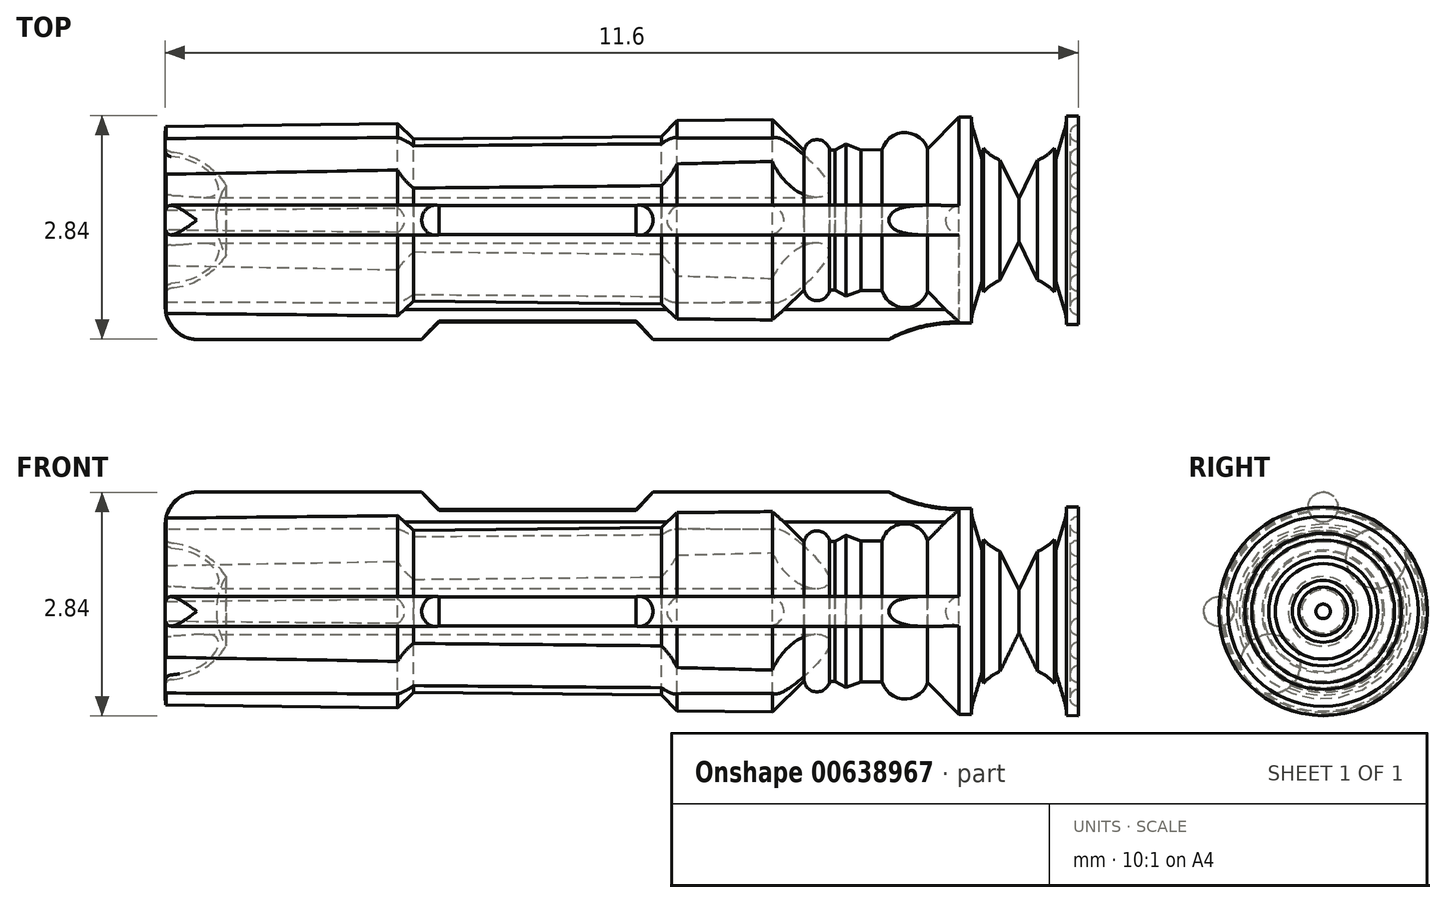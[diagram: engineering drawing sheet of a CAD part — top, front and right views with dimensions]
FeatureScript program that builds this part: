
annotation { "Feature Type Name" : "Feature", "Feature Type Description" : "" }
export const myFeature = defineFeature(function(context is Context, id is Id, definition is map)
    precondition{}
    {
        {
            var Q0;
            Q0=qCreatedBy(makeId("Top.planeOp"),FACE);
            var sketch = newSketch(context, id + "F0", { "sketchPlane" : qUnion([Q0])});
            skLineSegment(sketch, "E0", {"start": v(0, 6) * mm, "end": v(0, -4.69) * mm});
            skLineSegment(sketch, "E1", {"start": v(0, 6) * mm, "end": v(1.33, 6) * mm});
            skLineSegment(sketch, "E2", {"start": v(1.33, 6) * mm, "end": v(1.3, 4.48) * mm});
            skLineSegment(sketch, "E3", {"start": v(1.2, -5.6) * mm, "end": v(0.95, -5.6) * mm});
            skArc(sketch, "E4", {"start": v(0.87, -5.52) * mm, "mid": v(0.74, -5.12) * mm, "end": v(0.44, -4.83) * mm});
            skLineSegment(sketch, "E5", {"start": v(0.87, -5.6) * mm, "end": v(0, -5.6) * mm, "construction": true});
            skLineSegment(sketch, "E6", {"start": v(0, -4.69) * mm, "end": v(0, -4.95) * mm});
            skPoint(sketch, "E7.visualSharp", {"position": v(0.87, -5.6) * mm});
            skArc(sketch, "E7.filletArc", {"start": v(0.87, -5.52) * mm, "mid": v(0.9, -5.58) * mm, "end": v(0.95, -5.6) * mm});
            skLineSegment(sketch, "E8", {"start": v(0, 0) * mm, "end": v(1.26, 0) * mm, "construction": true});
            skArc(sketch, "E9", {"start": v(0, -4.95) * mm, "mid": v(0.23, -4.92) * mm, "end": v(0.44, -4.83) * mm});
            skLineSegment(sketch, "E10", {"start": v(0, -4.95) * mm, "end": v(0, -5.6) * mm, "construction": true});
            skArc(sketch, "E11", {"start": v(0.44, -4.83) * mm, "mid": v(0.23, -4.73) * mm, "end": v(0, -4.69) * mm, "construction": true});
            skArc(sketch, "E12", {"start": v(0.44, -4.83) * mm, "mid": v(0.52, -4.77) * mm, "end": v(0.59, -4.72) * mm, "construction": true});
            skArc(sketch, "E13", {"start": v(0.1, 6) * mm, "mid": v(0.2, 5.9) * mm, "end": v(0.3, 6) * mm});
            skArc(sketch, "E14.1.0.0", {"start": v(0.4, 6) * mm, "mid": v(0.5, 5.9) * mm, "end": v(0.6, 6) * mm});
            skArc(sketch, "E14.2.0.0", {"start": v(0.7, 6) * mm, "mid": v(0.8, 5.9) * mm, "end": v(0.9, 6) * mm});
            skArc(sketch, "E14.3.0.0", {"start": v(1, 6) * mm, "mid": v(1.1, 5.9) * mm, "end": v(1.2, 6) * mm});
            skLineSegment(sketch, "E14.direction1", {"start": v(0.1, 6) * mm, "end": v(0.4, 6) * mm, "construction": true});
            skArc(sketch, "E15.0", {"start": v(1, -5.2) * mm, "mid": v(0.77, -4.84) * mm, "end": v(0.43, -4.6) * mm, "construction": true});
            skLineSegment(sketch, "E15.1", {"start": v(1.12, 5.8) * mm, "end": v(1.1, 4.28) * mm, "construction": true});
            skArc(sketch, "E15.2", {"start": v(0.2, -4.72) * mm, "mid": v(0.32, -4.67) * mm, "end": v(0.43, -4.6) * mm, "construction": true});
            skLineSegment(sketch, "E16.0", {"start": v(0.92, 5.8) * mm, "end": v(0.9, 4.09) * mm, "construction": true});
            skLineSegment(sketch, "E17", {"start": v(1.23, -2.65) * mm, "end": v(1.03, -2.45) * mm});
            skLineSegment(sketch, "E18", {"start": v(1.06, 0.7) * mm, "end": v(1.27, 0.9) * mm});
            skLineSegment(sketch, "E19", {"start": v(1.03, -2.45) * mm, "end": v(1, -5.2) * mm, "construction": true});
            skLineSegment(sketch, "E20", {"start": v(1.06, 0.7) * mm, "end": v(1.03, -2.45) * mm});
            skLineSegment(sketch, "E21", {"start": v(1.23, -2.65) * mm, "end": v(1.2, -5.6) * mm});
            skLineSegment(sketch, "E22", {"start": v(1.27, 0.9) * mm, "end": v(1.23, -2.65) * mm, "construction": true});
            skLineSegment(sketch, "E23", {"start": v(1.28, 2.11) * mm, "end": v(1.08, 2.32) * mm});
            skLineSegment(sketch, "E24", {"start": v(1.3, 4.48) * mm, "end": v(1.1, 4.28) * mm});
            skLineSegment(sketch, "E25", {"start": v(0.88, 2.52) * mm, "end": v(0.8, -5.13) * mm, "construction": true});
            skLineSegment(sketch, "E26", {"start": v(0.9, 4.09) * mm, "end": v(0.9, 3.24) * mm});
            skLineSegment(sketch, "E27", {"start": v(1.08, 2.32) * mm, "end": v(0.88, 2.52) * mm});
            skLineSegment(sketch, "E28", {"start": v(1.1, 4.28) * mm, "end": v(0.9, 4.09) * mm});
            skLineSegment(sketch, "E29", {"start": v(1.08, 2.32) * mm, "end": v(1.06, 0.7) * mm, "construction": true});
            skLineSegment(sketch, "E30", {"start": v(1.1, 4.28) * mm, "end": v(1.08, 2.32) * mm, "construction": true});
            skLineSegment(sketch, "E31", {"start": v(1.28, 2.11) * mm, "end": v(1.27, 0.9) * mm});
            skLineSegment(sketch, "E32", {"start": v(1.3, 4.48) * mm, "end": v(1.28, 2.11) * mm, "construction": true});
            skArc(sketch, "E33", {"start": v(0.88, 2.52) * mm, "mid": v(1.02, 2.68) * mm, "end": v(0.89, 2.84) * mm});
            skArc(sketch, "E34", {"start": v(0.9, 3.5) * mm, "mid": v(1.11, 3.8) * mm, "end": v(0.9, 4.09) * mm});
            skLineSegment(sketch, "E35", {"start": v(0.89, 2.91) * mm, "end": v(0.89, 2.84) * mm});
            skLineSegment(sketch, "E36", {"start": v(0.97, 3.05) * mm, "end": v(0.89, 2.91) * mm});
            skLineSegment(sketch, "E37", {"start": v(0.9, 3.24) * mm, "end": v(0.97, 3.05) * mm});
            skLineSegment(sketch, "E38", {"start": v(0.89, 2.84) * mm, "end": v(0.88, 2.52) * mm});
            skSolve(sketch);
        }
        {
            var Q0;
            {var subQ5=sQuery(id+"F0.wireOp",EDGE,"E0");Q0=makeQuery(id+"F0.imprint","IMPRINT",FACE,{"disambiguationData":[TD([[makeQuery(id+"F0.imprint","IMPRINT",EDGE,{"derivedFrom":subQ5}),1.0]])]});}
            var Q1;
            Q1=makeQuery(id+"F0.imprint","IMPRINT",FACE,{"disambiguationData":[TD([[makeQuery(id+"F0.imprint","IMPRINT",EDGE,{"derivedFrom":sQuery(id+"F0.wireOp",EDGE,"E33")}),1.0]])]});
            var Q2;
            {var subQ0=sQuery(id+"F0.wireOp",EDGE,"E34");Q2=makeQuery(id+"F0.imprint","IMPRINT",FACE,{"disambiguationData":[TD([[makeQuery(id+"F0.imprint","IMPRINT",EDGE,{"derivedFrom":subQ0}),1.0]])]});}
            var Q3;
            Q3=sQuery(id+"F0.wireOp",EDGE,"E0");
            revolve(context, id + "F1", {"entities" : qUnion([Q0, Q1, Q2]), "axis" : qUnion([Q3]), "revolveType" : RevolveType.FULL});
        }
        {
            var Q0;
            Q0=qCreatedBy(makeId("Front.planeOp"),FACE);
            var sketch = newSketch(context, id + "F2", { "sketchPlane" : qUnion([Q0])});
            skLineSegment(sketch, "E39", {"start": v(0, 0) * mm, "end": v(0, 0.95) * mm, "construction": true});
            skLineSegment(sketch, "E40", {"start": v(0, 0) * mm, "end": v(-1.33, 0) * mm, "construction": true});
            skArc(sketch, "E41", {"start": v(-0.95, 0) * mm, "mid": v(-0.87, 0.36) * mm, "end": v(-0.67, 0.67) * mm, "construction": true});
            skArc(sketch, "E42", {"start": v(0, 0.95) * mm, "mid": v(0.67, -0.67) * mm, "end": v(-0.95, 0) * mm, "construction": true});
            skArc(sketch, "E43", {"start": v(0, 1.33) * mm, "mid": v(0.94, -0.94) * mm, "end": v(-1.33, 0) * mm, "construction": true});
            skArc(sketch, "E44", {"start": v(-1.33, 0) * mm, "mid": v(-1.22, 0.5) * mm, "end": v(-0.94, 0.94) * mm, "construction": true});
            skLineSegment(sketch, "E45", {"start": v(0, 0) * mm, "end": v(-0.94, 0.94) * mm, "construction": true});
            skArc(sketch, "E46", {"start": v(-0.94, 0.94) * mm, "mid": v(-0.5, 1.22) * mm, "end": v(0, 1.33) * mm, "construction": true});
            skArc(sketch, "E47", {"start": v(-0.67, 0.67) * mm, "mid": v(-0.36, 0.87) * mm, "end": v(0, 0.95) * mm, "construction": true});
            skCircle(sketch, "E48", {"center": v(-0.67, 0.67) * mm, "radius": 0.38 * mm});
            skCircle(sketch, "E49.MirrorC", {"center": v(0.67, 0.67) * mm, "radius": 0.38 * mm});
            skCircle(sketch, "E50.MirrorC", {"center": v(-0.67, -0.67) * mm, "radius": 0.38 * mm});
            skCircle(sketch, "E51.MirrorC", {"center": v(0.67, -0.67) * mm, "radius": 0.38 * mm});
            skCircle(sketch, "E52", {"center": v(0, 1.33) * mm, "radius": 0.19 * mm});
            skLineSegment(sketch, "E53", {"start": v(0, 0.95) * mm, "end": v(0, 1.33) * mm, "construction": true});
            skPoint(sketch, "E54", {"position": v(0, 1.14) * mm});
            skCircle(sketch, "E55.MirrorC", {"center": v(0, -1.33) * mm, "radius": 0.19 * mm});
            skCircle(sketch, "E56.MirrorC", {"center": v(-1.33, 0) * mm, "radius": 0.19 * mm});
            skCircle(sketch, "E57.MirrorC", {"center": v(1.33, 0) * mm, "radius": 0.19 * mm});
            skSolve(sketch);
        }
        {
            var Q0;
            Q0=makeQuery(id+"F2.imprint","IMPRINT",FACE,{"disambiguationData":[TD([[makeQuery(id+"F2.imprint","IMPRINT",EDGE,{"derivedFrom":sQuery(id+"F2.wireOp",EDGE,"E48")}),1.0]])]});
            var Q1;
            Q1=makeQuery(id+"F2.imprint","IMPRINT",FACE,{"disambiguationData":[TD([[makeQuery(id+"F2.imprint","IMPRINT",EDGE,{"derivedFrom":sQuery(id+"F2.wireOp",EDGE,"E49.MirrorC")}),-1.0]])]});
            var Q2;
            Q2=makeQuery(id+"F2.imprint","IMPRINT",FACE,{"disambiguationData":[TD([[makeQuery(id+"F2.imprint","IMPRINT",EDGE,{"derivedFrom":sQuery(id+"F2.wireOp",EDGE,"E51.MirrorC")}),1.0]])]});
            var Q3;
            Q3=makeQuery(id+"F2.imprint","IMPRINT",FACE,{"disambiguationData":[TD([[makeQuery(id+"F2.imprint","IMPRINT",EDGE,{"derivedFrom":sQuery(id+"F2.wireOp",EDGE,"E50.MirrorC")}),-1.0]])]});
            var Q4;
            Q4=makeQuery(id+"F1.opRevolve","SWEPT_FACE",FACE,{"disambiguationData":[OSD([sQuery(id+"F0.wireOp",EDGE,"E3")])]});
            var Q5;
            Q5=makeQuery(id+"F1.opRevolve","SWEPT_FACE",FACE,{"disambiguationData":[OSD([sQuery(id+"F0.wireOp",EDGE,"E23"),sQuery(id+"F0.wireOp",EDGE,"E27")])]});
            extrude(context, id + "F3", {"entities" : qUnion([Q0, Q1, Q2, Q3]), "operationType" : NewBodyOperationType.REMOVE, "endBound" : BoundingType.UP_TO_SURFACE, "endBoundEntityFace" : qUnion([Q4]), "depth" : 5.84 * mm, "hasSecondDirection" : true, "secondDirectionBound" : SecondDirectionBoundingType.UP_TO_SURFACE, "secondDirectionOppositeDirection" : true, "secondDirectionBoundEntityFace" : qUnion([Q5]), "secondDirectionDepth" : 2.4 * mm});
        }
        {
            var Q0;
            Q0=makeQuery(id+"F2.imprint","IMPRINT",FACE,{"disambiguationData":[TD([[makeQuery(id+"F2.imprint","IMPRINT",EDGE,{"derivedFrom":sQuery(id+"F2.wireOp",EDGE,"E56.MirrorC")}),-1.0]])]});
            var Q1;
            Q1=makeQuery(id+"F2.imprint","IMPRINT",FACE,{"disambiguationData":[TD([[makeQuery(id+"F2.imprint","IMPRINT",EDGE,{"derivedFrom":sQuery(id+"F2.wireOp",EDGE,"E55.MirrorC")}),-1.0]])]});
            var Q2;
            Q2=makeQuery(id+"F2.imprint","IMPRINT",FACE,{"disambiguationData":[TD([[makeQuery(id+"F2.imprint","IMPRINT",EDGE,{"derivedFrom":sQuery(id+"F2.wireOp",EDGE,"E57.MirrorC")}),1.0]])]});
            var Q3;
            Q3=makeQuery(id+"F2.imprint","IMPRINT",FACE,{"disambiguationData":[TD([[makeQuery(id+"F2.imprint","IMPRINT",EDGE,{"derivedFrom":sQuery(id+"F2.wireOp",EDGE,"E52")}),1.0]])]});
            var Q4;
            Q4=makeQuery(id+"F3.boolean.opBoolean","SPLIT",FACE,{"disambiguationData":[TD([makeQuery(id+"F1.opRevolve","SWEPT_FACE",FACE,{"disambiguationData":[OSD([sQuery(id+"F0.wireOp",EDGE,"E7.filletArc")])]}),makeQuery(id+"F1.opRevolve","SWEPT_FACE",FACE,{"disambiguationData":[OSD([sQuery(id+"F0.wireOp",EDGE,"E21")])]}),makeQuery(id+"F3.opExtrude","SWEPT_FACE",FACE,{"disambiguationData":[OSD([sQuery(id+"F2.wireOp",EDGE,"E48")])]}),makeQuery(id+"F3.opExtrude","SWEPT_FACE",FACE,{"disambiguationData":[OSD([sQuery(id+"F2.wireOp",EDGE,"E49.MirrorC")])]})])],"derivedFrom":makeQuery(id+"F1.opRevolve","SWEPT_FACE",FACE,{"disambiguationData":[OSD([sQuery(id+"F0.wireOp",EDGE,"E3")])]})});
            var Q5;
            Q5=makeQuery(id+"F1.opRevolve","SWEPT_FACE",FACE,{"disambiguationData":[OSD([sQuery(id+"F0.wireOp",EDGE,"E24"),sQuery(id+"F0.wireOp",EDGE,"E28")])]});
            extrude(context, id + "F4", {"entities" : qUnion([Q0, Q1, Q2, Q3]), "operationType" : NewBodyOperationType.ADD, "endBound" : BoundingType.UP_TO_SURFACE, "endBoundEntityFace" : qUnion([Q4]), "depth" : 25 * mm, "hasSecondDirection" : true, "secondDirectionBound" : SecondDirectionBoundingType.UP_TO_SURFACE, "secondDirectionOppositeDirection" : true, "secondDirectionBoundEntityFace" : qUnion([Q5]), "secondDirectionDepth" : 25 * mm});
        }
        {
            var Q0;
            Q0=qCreatedBy(makeId("Top.planeOp"),FACE);
            var sketch = newSketch(context, id + "F5", { "sketchPlane" : qUnion([Q0])});
            skLineSegment(sketch, "E58.0", {"start": v(-1.33, 6) * mm, "end": v(1.33, 6) * mm});
            skLineSegment(sketch, "E59", {"start": v(1.33, 6) * mm, "end": v(1.32, 5.85) * mm});
            skLineSegment(sketch, "E60", {"start": v(1.51, 4.68) * mm, "end": v(1.51, 3.6) * mm, "construction": true});
            skLineSegment(sketch, "E61", {"start": v(0, 0) * mm, "end": v(0, 6) * mm});
            skLineSegment(sketch, "E62", {"start": v(0, 0) * mm, "end": v(0, -5.6) * mm});
            skLineSegment(sketch, "E63.0", {"start": v(0, -5.6) * mm, "end": v(1.11, -5.6) * mm});
            skPoint(sketch, "E64.orphan", {"position": v(0.13, -5.6) * mm});
            skPoint(sketch, "E65.orphan", {"position": v(0.58, -5.6) * mm});
            skPoint(sketch, "E66.visualSharp", {"position": v(1.51, -5.6) * mm});
            skArc(sketch, "E66.filletArc", {"start": v(1.11, -5.6) * mm, "mid": v(1.4, -5.48) * mm, "end": v(1.51, -5.2) * mm});
            skLineSegment(sketch, "E67", {"start": v(1.51, -2.34) * mm, "end": v(1.51, -5.2) * mm});
            skLineSegment(sketch, "E68", {"start": v(1.51, 0.6) * mm, "end": v(1.51, -2.34) * mm, "construction": true});
            skLineSegment(sketch, "E69", {"start": v(1.51, -2.34) * mm, "end": v(1.3, -2.12) * mm});
            skLineSegment(sketch, "E70", {"start": v(1.3, -2.12) * mm, "end": v(1.3, 0.38) * mm});
            skLineSegment(sketch, "E71", {"start": v(1.3, 0.38) * mm, "end": v(1.51, 0.6) * mm});
            skArc(sketch, "E72", {"start": v(1.3, 4.49) * mm, "mid": v(1.36, 4.03) * mm, "end": v(1.51, 3.6) * mm});
            skLineSegment(sketch, "E73", {"start": v(1.51, 3.6) * mm, "end": v(1.51, 0.6) * mm});
            skArc(sketch, "E74", {"start": v(1.32, 5.85) * mm, "mid": v(0.71, 5.25) * mm, "end": v(1.3, 4.64) * mm});
            skLineSegment(sketch, "E75", {"start": v(1.3, 4.64) * mm, "end": v(1.3, 4.49) * mm});
            skLineSegment(sketch, "E76", {"start": v(1.32, 5.85) * mm, "end": v(1.3, 4.64) * mm, "construction": true});
            skLineSegment(sketch, "E77", {"start": v(1.14, 4.67) * mm, "end": v(1.14, 5.82) * mm, "construction": true});
            skLineSegment(sketch, "E78", {"start": v(1.14, 4.67) * mm, "end": v(0.78, 4.78) * mm});
            skLineSegment(sketch, "E79", {"start": v(0.78, 4.78) * mm, "end": v(1.14, 4.82) * mm});
            skLineSegment(sketch, "E80", {"start": v(1.14, 4.82) * mm, "end": v(0.78, 5) * mm});
            skLineSegment(sketch, "E81", {"start": v(0.27, 5.25) * mm, "end": v(1.14, 5.67) * mm});
            skLineSegment(sketch, "E82", {"start": v(1.14, 5.67) * mm, "end": v(0.78, 5.71) * mm});
            skLineSegment(sketch, "E83", {"start": v(0.78, 5.71) * mm, "end": v(1.14, 5.82) * mm});
            skLineSegment(sketch, "E84", {"start": v(0.27, 5.25) * mm, "end": v(1.32, 5.25) * mm, "construction": true});
            skLineSegment(sketch, "E85", {"start": v(0.78, 4.78) * mm, "end": v(0.78, 5) * mm, "construction": true});
            skLineSegment(sketch, "E86", {"start": v(0.78, 5.25) * mm, "end": v(0.78, 5.5) * mm, "construction": true});
            skLineSegment(sketch, "E87", {"start": v(0.78, 5) * mm, "end": v(0.27, 5.25) * mm});
            skLineSegment(sketch, "E88", {"start": v(0.78, 5.5) * mm, "end": v(0.78, 5.71) * mm, "construction": true});
            skLineSegment(sketch, "E89", {"start": v(0.78, 5) * mm, "end": v(0.78, 5.25) * mm, "construction": true});
            skSolve(sketch);
        }
        {
            var Q0;
            {var subQ14=sQuery(id+"F5.wireOp",EDGE,"E59");Q0=makeQuery(id+"F5.imprint","IMPRINT",FACE,{"disambiguationData":[TD([[makeQuery(id+"F5.imprint","IMPRINT",EDGE,{"derivedFrom":subQ14}),-1.0]])]});}
            var Q1;
            Q1=sQuery(id+"F5.wireOp",EDGE,"E61");
            revolve(context, id + "F6", {"operationType" : NewBodyOperationType.INTERSECT, "entities" : qUnion([Q0]), "axis" : qUnion([Q1]), "revolveType" : RevolveType.FULL});
        }
        {
            var Q0;
            Q0=makeQuery(id+"F1.opRevolve","SWEPT_BODY",BODY,{"disambiguationData":[OSD([sQuery(id+"F0.wireOp",EDGE,"E0"),sQuery(id+"F0.wireOp",EDGE,"E1"),sQuery(id+"F0.wireOp",EDGE,"E2"),sQuery(id+"F0.wireOp",EDGE,"E3"),sQuery(id+"F0.wireOp",EDGE,"E4"),sQuery(id+"F0.wireOp",EDGE,"E6"),sQuery(id+"F0.wireOp",EDGE,"E7.filletArc"),sQuery(id+"F0.wireOp",EDGE,"E9"),sQuery(id+"F0.wireOp",EDGE,"E13"),sQuery(id+"F0.wireOp",EDGE,"E14.1.0.0"),sQuery(id+"F0.wireOp",EDGE,"E14.2.0.0"),sQuery(id+"F0.wireOp",EDGE,"E14.3.0.0"),sQuery(id+"F0.wireOp",EDGE,"E17"),sQuery(id+"F0.wireOp",EDGE,"E18"),sQuery(id+"F0.wireOp",EDGE,"E20"),sQuery(id+"F0.wireOp",EDGE,"E21"),sQuery(id+"F0.wireOp",EDGE,"E23"),sQuery(id+"F0.wireOp",EDGE,"E24"),sQuery(id+"F0.wireOp",EDGE,"E26"),sQuery(id+"F0.wireOp",EDGE,"E27"),sQuery(id+"F0.wireOp",EDGE,"E28"),sQuery(id+"F0.wireOp",EDGE,"E31"),sQuery(id+"F0.wireOp",EDGE,"E33"),sQuery(id+"F0.wireOp",EDGE,"E34"),sQuery(id+"F0.wireOp",EDGE,"E35"),sQuery(id+"F0.wireOp",EDGE,"E36"),sQuery(id+"F0.wireOp",EDGE,"E37")])]});
            var Q1;
            Q1=sQuery(id+"F2.wireOp",EDGE,"E39");
            transform(context, id + "F7", {"entities" : qUnion([Q0]), "transformType" : TransformType.ROTATION, "transformAxis" : qUnion([Q1]), "angle" : 90 * degree, "oppositeDirection" : true, "makeCopy" : false});
        }
    });
